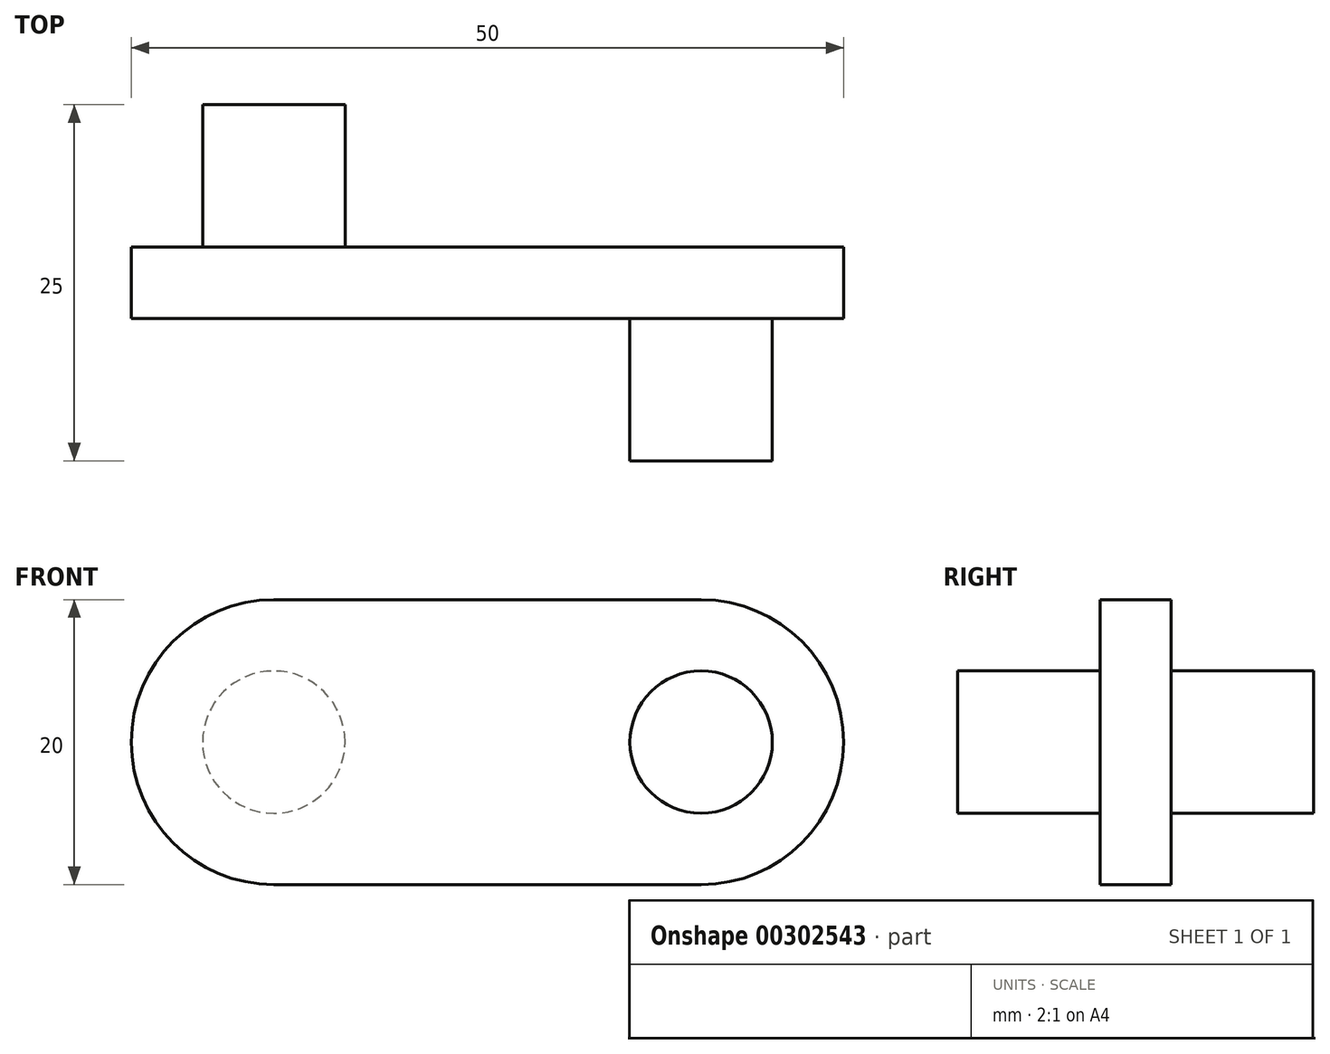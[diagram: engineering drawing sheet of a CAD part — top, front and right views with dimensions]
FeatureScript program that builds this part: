
annotation { "Feature Type Name" : "Feature", "Feature Type Description" : "" }
export const myFeature = defineFeature(function(context is Context, id is Id, definition is map)
    precondition{}
    {
        {
            var Q0;
            Q0=qCreatedBy(makeId("Front.planeOp"),FACE);
            var sketch = newSketch(context, id + "F0", { "sketchPlane" : qUnion([Q0])});
            skLineSegment(sketch, "E0", {"start": v(0, 0) * mm, "end": v(30, 0) * mm});
            skLineSegment(sketch, "E1", {"start": v(0, 20) * mm, "end": v(30, 20) * mm});
            skArc(sketch, "E2", {"start": v(30, 0) * mm, "mid": v(40, 10) * mm, "end": v(30, 20) * mm});
            skArc(sketch, "E3", {"start": v(0, 20) * mm, "mid": v(-10, 10) * mm, "end": v(0, 0) * mm});
            skSolve(sketch);
        }
        {
            var Q0;
            Q0=makeQuery(id+"F0.imprint","IMPRINT",FACE,{"disambiguationData":[TD([[makeQuery(id+"F0.imprint","IMPRINT",EDGE,{"derivedFrom":sQuery(id+"F0.wireOp",EDGE,"E0")}),1.0]])]});
            extrude(context, id + "F1", {"entities" : qUnion([Q0]), "depth" : 5 * mm});
        }
        {
            var Q0;
            Q0=makeQuery(id+"F1.opExtrude","CAP_FACE",FACE,{"disambiguationData":[OSD([sQuery(id+"F0.wireOp",EDGE,"E0"),sQuery(id+"F0.wireOp",EDGE,"E1"),sQuery(id+"F0.wireOp",EDGE,"E2"),sQuery(id+"F0.wireOp",EDGE,"E3")])],"isStart":false});
            var sketch = newSketch(context, id + "F2", { "sketchPlane" : qUnion([Q0])});
            skCircle(sketch, "E4", {"center": v(30, 10) * mm, "radius": 5 * mm});
            skSolve(sketch);
        }
        {
            var Q0;
            Q0 = qSketchRegion(id + "F2", true);
            extrude(context, id + "F3", {"entities" : qUnion([Q0]), "operationType" : NewBodyOperationType.ADD, "depth" : 10 * mm});
        }
        {
            var Q0;
            Q0=makeQuery(id+"F0.imprint","IMPRINT",FACE,{"disambiguationData":[TD([[makeQuery(id+"F0.imprint","IMPRINT",EDGE,{"derivedFrom":sQuery(id+"F0.wireOp",EDGE,"E0")}),1.0]])]});
            var sketch = newSketch(context, id + "F4", { "sketchPlane" : qUnion([Q0])});
            skCircle(sketch, "E5", {"center": v(0, 10) * mm, "radius": 5 * mm});
            skSolve(sketch);
        }
        {
            var Q0;
            Q0=makeQuery(id+"F4.imprint","IMPRINT",FACE,{"disambiguationData":[TD([[makeQuery(id+"F4.imprint","IMPRINT",EDGE,{"derivedFrom":sQuery(id+"F4.wireOp",EDGE,"E5")}),1.0]])]});
            var Q1;
            Q1=sQuery(id+"F4.wireOp",EDGE,"E5");
            extrude(context, id + "F5", {"entities" : qUnion([Q0]), "operationType" : NewBodyOperationType.ADD, "surfaceEntities" : qUnion([Q1]), "oppositeDirection" : true, "depth" : 10 * mm});
        }
    });
